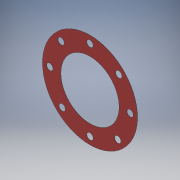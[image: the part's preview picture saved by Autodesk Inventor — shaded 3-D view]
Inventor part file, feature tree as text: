
AUTODESK INVENTOR PART (.ipt)
format: ipt  version: 2017 (Build 210142000, 142)  size: 132,608 bytes
history: native  units: mm
features: extrude x1, sketch x1
ambient origin geometry x8: Origin, YZ Plane, XZ Plane, XY Plane, X Axis, Y Axis, Z Axis, Center Point
bodies: Body1 (feature_tree)
feature tree (2):
  extrude  "Extrusion2"  Depth=0.1mm
  sketch  "Sketch1"  dims[d0=52.0mm d1=32.0mm d2=44.0mm d21=3.5mm d22=3.5mm d23=3.5mm d24=3.5mm d25=3.5mm d26=3.5mm d27=3.5mm d28=3.5mm d29=0.1mm d30=0.0mm]
